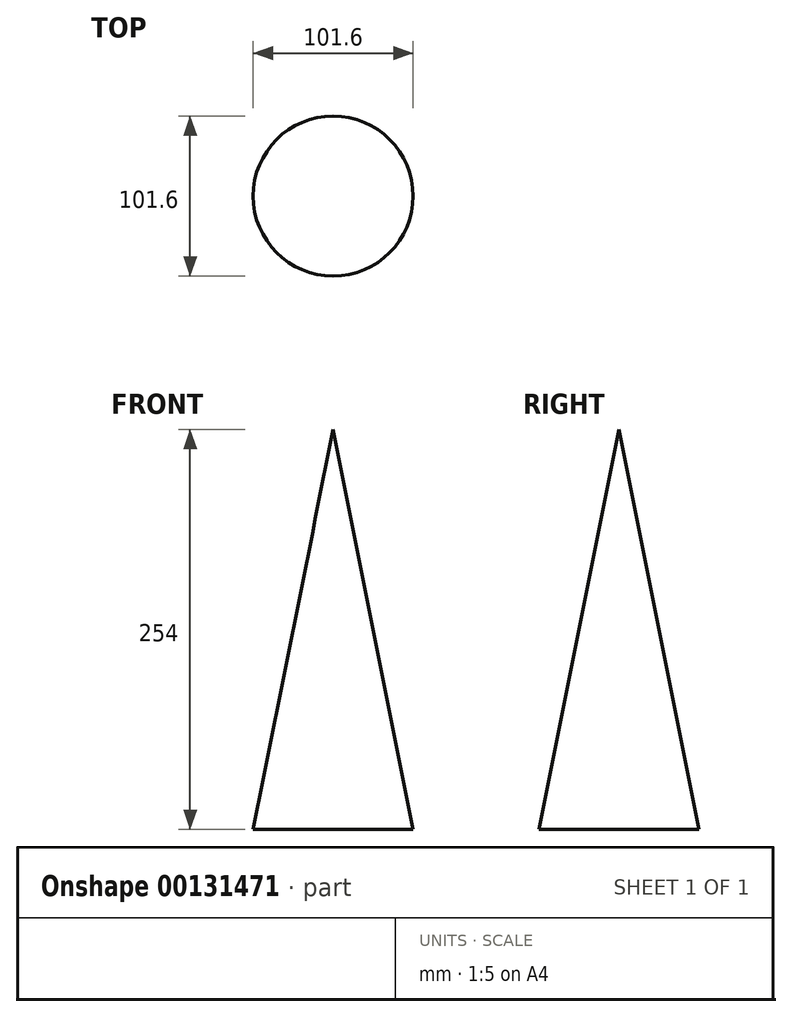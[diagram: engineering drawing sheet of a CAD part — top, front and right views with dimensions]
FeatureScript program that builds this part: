
annotation { "Feature Type Name" : "Feature", "Feature Type Description" : "" }
export const myFeature = defineFeature(function(context is Context, id is Id, definition is map)
    precondition{}
    {
        {
            var Q0;
            Q0=qCreatedBy(makeId("Front.planeOp"),FACE);
            var sketch = newSketch(context, id + "F0", { "sketchPlane" : qUnion([Q0])});
            skLineSegment(sketch, "E0", {"start": v(0, 254) * mm, "end": v(-50.8, 0) * mm});
            skLineSegment(sketch, "E1", {"start": v(0, 254) * mm, "end": v(0, 0) * mm});
            skLineSegment(sketch, "E2", {"start": v(-50.8, 0) * mm, "end": v(0, 0) * mm});
            skSolve(sketch);
        }
        {
            var Q0;
            Q0 = qSketchRegion(id + "F0", true);
            var Q1;
            Q1=sQuery(id+"F0.wireOp",EDGE,"E1");
            revolve(context, id + "F1", {"entities" : qUnion([Q0]), "axis" : qUnion([Q1]), "revolveType" : RevolveType.FULL});
        }
    });
